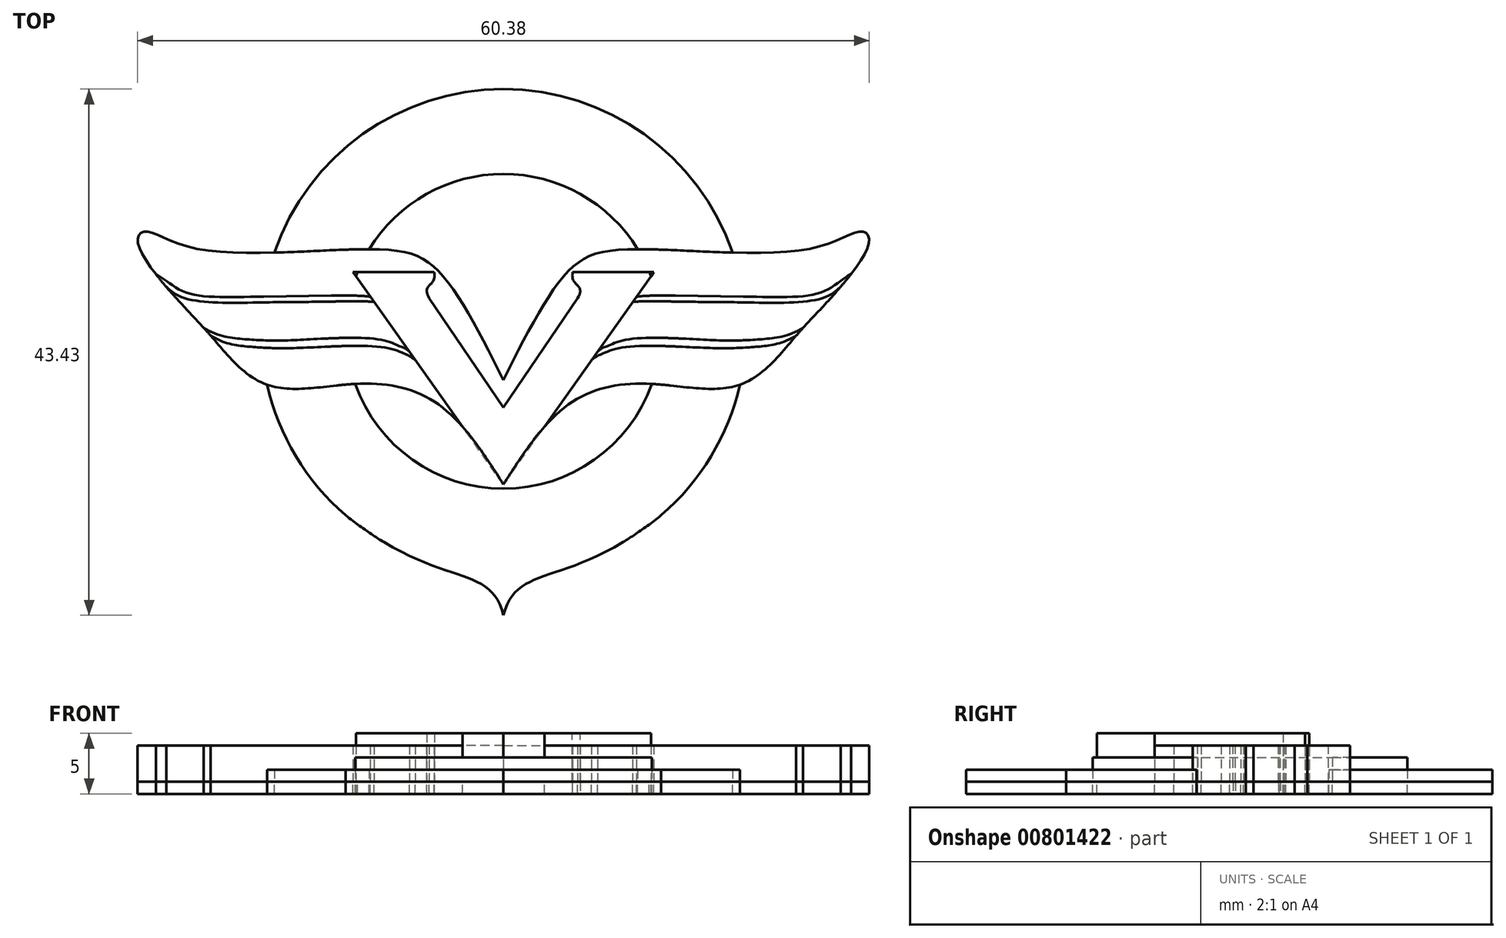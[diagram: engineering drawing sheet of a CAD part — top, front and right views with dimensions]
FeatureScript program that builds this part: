
annotation { "Feature Type Name" : "Feature", "Feature Type Description" : "" }
export const myFeature = defineFeature(function(context is Context, id is Id, definition is map)
    precondition{}
    {
        {
            var Q0;
            Q0=qCreatedBy(makeId("Top.planeOp"),FACE);
            var sketch = newSketch(context, id + "F0", { "sketchPlane" : qUnion([Q0])});
            skCircle(sketch, "E0", {"center": v(31.17, -29.1) * mm, "radius": 20 * mm});
            skFitSpline(sketch, "E1", {"points": [v(31.17, -52.52) * mm, v(44.19, -44.27) * mm], "startDerivative": vector(3.45, 13.39) * mm, "endDerivative": vector(23.34, 18.74) * mm});
            skLineSegment(sketch, "E2", {"start": v(31.17, -52.52) * mm, "end": v(31.17, -29.1) * mm, "construction": true});
            skFitSpline(sketch, "E3.MirrorCS", {"points": [v(31.17, -52.52) * mm, v(18.15, -44.27) * mm], "startDerivative": vector(-3.45, 13.39) * mm, "endDerivative": vector(-23.34, 18.74) * mm});
            skFitSpline(sketch, "E4", {"points": [v(31.17, -33.12) * mm, v(36.42, -24.23) * mm, v(41.17, -22.33) * mm, v(56.67, -22.23) * mm, v(60.84, -20.86) * mm, v(61.35, -21.69) * mm, v(58.45, -26.04) * mm, v(55.24, -29.56) * mm, v(50.68, -33.5) * mm, v(43.26, -33.42) * mm, v(36.77, -34.96) * mm, v(31.17, -41.74) * mm], "startDerivative": vector(45.4, 90.85) * mm, "endDerivative": vector(-47.74, -76.75) * mm});
            skFitSpline(sketch, "E5", {"points": [v(42.15, -26.23) * mm, v(45.57, -26.14) * mm, v(52.5, -26.25) * mm, v(57.51, -25.84) * mm, v(59.86, -24.36) * mm], "startDerivative": vector(15.57, 1.58) * mm, "endDerivative": vector(13.88, 7.6) * mm});
            skFitSpline(sketch, "E6", {"points": [v(38.94, -30.77) * mm, v(39.65, -30.35) * mm, v(41.5, -29.75) * mm, v(48.88, -29.83) * mm, v(52.47, -29.74) * mm, v(55.9, -28.8) * mm], "startDerivative": vector(9.68, 8.92) * mm, "endDerivative": vector(17.36, 10.5) * mm});
            skFitSpline(sketch, "E7.MirrorCS", {"points": [v(31.17, -33.12) * mm, v(25.92, -24.23) * mm, v(21.17, -22.33) * mm, v(5.67, -22.23) * mm, v(1.5, -20.86) * mm, v(0.99, -21.69) * mm, v(3.9, -26.04) * mm, v(7.1, -29.56) * mm, v(11.66, -33.5) * mm, v(19.08, -33.42) * mm, v(25.57, -34.96) * mm, v(31.17, -41.74) * mm], "startDerivative": vector(-45.4, 90.85) * mm, "endDerivative": vector(47.74, -76.75) * mm});
            skFitSpline(sketch, "E8.MirrorCS", {"points": [v(23.4, -30.77) * mm, v(22.69, -30.35) * mm, v(20.85, -29.75) * mm, v(13.46, -29.83) * mm, v(9.87, -29.74) * mm, v(6.43, -28.8) * mm], "startDerivative": vector(-9.68, 8.92) * mm, "endDerivative": vector(-17.36, 10.5) * mm});
            skFitSpline(sketch, "E9.MirrorCS", {"points": [v(20.19, -26.23) * mm, v(16.77, -26.14) * mm, v(9.84, -26.25) * mm, v(4.83, -25.84) * mm, v(2.48, -24.36) * mm], "startDerivative": vector(-15.57, 1.58) * mm, "endDerivative": vector(-13.88, 7.6) * mm});
            skCircle(sketch, "E10", {"center": v(31.17, -29.1) * mm, "radius": 13 * mm});
            skLineSegment(sketch, "E11", {"start": v(31.17, -41.74) * mm, "end": v(18.76, -24.2) * mm});
            skLineSegment(sketch, "E12", {"start": v(18.76, -24.2) * mm, "end": v(25.46, -24.2) * mm});
            skLineSegment(sketch, "E13", {"start": v(31.17, -35.37) * mm, "end": v(25.04, -26.35) * mm});
            skFitSpline(sketch, "E14", {"points": [v(25.04, -26.35) * mm, v(25.46, -24.2) * mm], "startDerivative": vector(-2.08, 3.7) * mm, "endDerivative": vector(-0.66, 3.78) * mm});
            skLineSegment(sketch, "E15.MirrorCS", {"start": v(31.17, -35.37) * mm, "end": v(37.3, -26.35) * mm});
            skFitSpline(sketch, "E16.MirrorCS", {"points": [v(37.3, -26.35) * mm, v(36.88, -24.2) * mm], "startDerivative": vector(2.08, 3.7) * mm, "endDerivative": vector(0.66, 3.78) * mm});
            skLineSegment(sketch, "E17.MirrorCS", {"start": v(43.58, -24.2) * mm, "end": v(36.88, -24.2) * mm});
            skLineSegment(sketch, "E18.MirrorCS", {"start": v(31.17, -41.74) * mm, "end": v(43.58, -24.2) * mm});
            skCircle(sketch, "E19", {"center": v(31.17, -29.1) * mm, "radius": 14.5 * mm});
            skLineSegment(sketch, "E20", {"start": v(31.17, -29.1) * mm, "end": v(31.17, -14.6) * mm, "construction": true});
            skFitSpline(sketch, "E21", {"points": [v(41.84, -26.66) * mm, v(45.46, -26.64) * mm, v(50.26, -26.69) * mm, v(56.4, -26.59) * mm, v(59.57, -24.74) * mm], "startDerivative": vector(15.57, 1.58) * mm, "endDerivative": vector(12.34, 17.15) * mm});
            skFitSpline(sketch, "E22", {"points": [v(38.44, -31.47) * mm, v(39.16, -31.02) * mm, v(41, -30.42) * mm, v(48.39, -30.47) * mm, v(51.98, -30.37) * mm, v(55.33, -29.45) * mm], "startDerivative": vector(9.65, 8.96) * mm, "endDerivative": vector(17.32, 10.56) * mm});
            skFitSpline(sketch, "E23.MirrorCS", {"points": [v(20.5, -26.66) * mm, v(16.88, -26.64) * mm, v(12.08, -26.69) * mm, v(5.95, -26.59) * mm, v(2.77, -24.74) * mm], "startDerivative": vector(-15.57, 1.58) * mm, "endDerivative": vector(-12.34, 17.15) * mm});
            skFitSpline(sketch, "E24.MirrorCS", {"points": [v(23.9, -31.47) * mm, v(23.18, -31.02) * mm, v(21.34, -30.42) * mm, v(13.95, -30.47) * mm, v(10.36, -30.37) * mm, v(7, -29.45) * mm], "startDerivative": vector(-9.65, 8.96) * mm, "endDerivative": vector(-17.32, 10.56) * mm});
            skSolve(sketch);
        }
        {
            var Q0;
            {var subQ0=sQuery(id+"F0.wireOp",EDGE,"E4");var subQ1=sQuery(id+"F0.wireOp",EDGE,"E0");var subQ2=makeQuery(id+"F0.imprint","INTERSECT",VERTEX,{"disambiguationData":[OD(0.0)],"derivedFrom":[subQ1,subQ0]});Q0=makeQuery(id+"F0.imprint","IMPRINT",FACE,{"disambiguationData":[TD([[makeQuery(id+"F0.imprint","IMPRINT",EDGE,{"disambiguationData":[TD([[subQ2,-1.0]])],"derivedFrom":subQ1}),1.0]])]});}
            var Q1;
            {var subQ1=sQuery(id+"F0.wireOp",EDGE,"E0");var subQ6=sQuery(id+"F0.wireOp",EDGE,"E3.MirrorCS");var subQ12=makeQuery(id+"F0.imprint","INTERSECT",VERTEX,{"disambiguationData":[OD(0.0)],"derivedFrom":[subQ1,subQ6]});Q1=makeQuery(id+"F0.imprint","IMPRINT",FACE,{"disambiguationData":[TD([[makeQuery(id+"F0.imprint","IMPRINT",EDGE,{"disambiguationData":[TD([[subQ12,1.0]])],"derivedFrom":subQ1}),1.0]])]});}
            var Q2;
            {var subQ0=sQuery(id+"F0.wireOp",EDGE,"E19");var subQ1=sQuery(id+"F0.wireOp",EDGE,"E4");var subQ2=makeQuery(id+"F0.imprint","INTERSECT",VERTEX,{"disambiguationData":[OD(1.0)],"derivedFrom":[subQ1,subQ0]});Q2=makeQuery(id+"F0.imprint","IMPRINT",FACE,{"disambiguationData":[TD([[makeQuery(id+"F0.imprint","IMPRINT",EDGE,{"disambiguationData":[TD([[subQ2,-1.0]])],"derivedFrom":subQ1}),1.0]])]});}
            var Q3;
            {var subQ0=sQuery(id+"F0.wireOp",EDGE,"E10");var subQ1=sQuery(id+"F0.wireOp",EDGE,"E4");var subQ2=makeQuery(id+"F0.imprint","INTERSECT",VERTEX,{"disambiguationData":[OD(0.0)],"derivedFrom":[subQ1,subQ0]});Q3=makeQuery(id+"F0.imprint","IMPRINT",FACE,{"disambiguationData":[TD([[makeQuery(id+"F0.imprint","IMPRINT",EDGE,{"disambiguationData":[TD([[subQ2,-1.0]])],"derivedFrom":subQ1}),1.0]])]});}
            var Q4;
            {var subQ0=sQuery(id+"F0.wireOp",EDGE,"E3.MirrorCS");var subQ1=sQuery(id+"F0.wireOp",EDGE,"E0");var subQ2=makeQuery(id+"F0.imprint","INTERSECT",VERTEX,{"disambiguationData":[OD(1.0)],"derivedFrom":[subQ1,subQ0]});Q4=makeQuery(id+"F0.imprint","IMPRINT",FACE,{"disambiguationData":[TD([[makeQuery(id+"F0.imprint","IMPRINT",EDGE,{"disambiguationData":[TD([[subQ2,-1.0]])],"derivedFrom":subQ1}),-1.0]])]});}
            extrude(context, id + "F1", {"entities" : qUnion([Q0, Q1, Q2, Q3, Q4]), "depth" : 1 * mm, "offsetDistance" : 25 * mm});
        }
        {
            var Q0;
            {var subQ0=sQuery(id+"F0.wireOp",EDGE,"E7.MirrorCS");var subQ1=sQuery(id+"F0.wireOp",EDGE,"E4");var subQ2=makeQuery(id+"F0.imprint","INTERSECT",VERTEX,{"derivedFrom":[subQ1,subQ0]});Q0=makeQuery(id+"F0.imprint","IMPRINT",FACE,{"disambiguationData":[TD([[makeQuery(id+"F0.imprint","IMPRINT",EDGE,{"disambiguationData":[TD([[subQ2,-1.0]])],"derivedFrom":subQ1}),1.0]])]});}
            var Q1;
            {var subQ0=sQuery(id+"F0.wireOp",EDGE,"E10");var subQ1=sQuery(id+"F0.wireOp",EDGE,"E4");var subQ2=makeQuery(id+"F0.imprint","INTERSECT",VERTEX,{"disambiguationData":[OD(1.0)],"derivedFrom":[subQ1,subQ0]});Q1=makeQuery(id+"F0.imprint","IMPRINT",FACE,{"disambiguationData":[TD([[makeQuery(id+"F0.imprint","IMPRINT",EDGE,{"disambiguationData":[TD([[subQ2,-1.0]])],"derivedFrom":subQ1}),1.0]])]});}
            var Q2;
            {var subQ0=sQuery(id+"F0.wireOp",EDGE,"E18.MirrorCS");var subQ1=sQuery(id+"F0.wireOp",EDGE,"E4");var subQ3=makeQuery(id+"F0.imprint","INTERSECT",VERTEX,{"derivedFrom":[subQ1,subQ0]});Q2=makeQuery(id+"F0.imprint","IMPRINT",FACE,{"disambiguationData":[TD([[makeQuery(id+"F0.imprint","IMPRINT",EDGE,{"disambiguationData":[TD([[subQ3,-1.0]])],"derivedFrom":subQ1}),1.0]])]});}
            var Q3;
            {var subQ0=sQuery(id+"F0.wireOp",EDGE,"E11");var subQ1=sQuery(id+"F0.wireOp",EDGE,"E7.MirrorCS");var subQ3=makeQuery(id+"F0.imprint","INTERSECT",VERTEX,{"derivedFrom":[subQ1,subQ0]});Q3=makeQuery(id+"F0.imprint","IMPRINT",FACE,{"disambiguationData":[TD([[makeQuery(id+"F0.imprint","IMPRINT",EDGE,{"disambiguationData":[TD([[subQ3,-1.0]])],"derivedFrom":subQ1}),-1.0]])]});}
            extrude(context, id + "F2", {"entities" : qUnion([Q0, Q1, Q2, Q3]), "depth" : 2 * mm, "offsetDistance" : 25 * mm});
        }
        {
            var Q0;
            Q0=makeQuery(id+"F0.imprint","IMPRINT",FACE,{"disambiguationData":[TD([[makeQuery(id+"F0.imprint","IMPRINT",EDGE,{"derivedFrom":sQuery(id+"F0.wireOp",EDGE,"E13")}),1.0]])]});
            extrude(context, id + "F3", {"entities" : qUnion([Q0]), "depth" : 4 * mm, "offsetDistance" : 25 * mm});
        }
        {
            var Q0;
            {var subQ0=sQuery(id+"F0.wireOp",EDGE,"E7.MirrorCS");var subQ1=sQuery(id+"F0.wireOp",EDGE,"E0");var subQ2=makeQuery(id+"F0.imprint","INTERSECT",VERTEX,{"disambiguationData":[OD(0.0)],"derivedFrom":[subQ1,subQ0]});Q0=makeQuery(id+"F0.imprint","IMPRINT",FACE,{"disambiguationData":[TD([[makeQuery(id+"F0.imprint","IMPRINT",EDGE,{"disambiguationData":[TD([[subQ2,-1.0]])],"derivedFrom":subQ1}),-1.0]])]});}
            var Q1;
            {var subQ0=sQuery(id+"F0.wireOp",EDGE,"E7.MirrorCS");var subQ1=sQuery(id+"F0.wireOp",EDGE,"E0");var subQ2=makeQuery(id+"F0.imprint","INTERSECT",VERTEX,{"disambiguationData":[OD(0.0)],"derivedFrom":[subQ1,subQ0]});Q1=makeQuery(id+"F0.imprint","IMPRINT",FACE,{"disambiguationData":[TD([[makeQuery(id+"F0.imprint","IMPRINT",EDGE,{"disambiguationData":[TD([[subQ2,-1.0]])],"derivedFrom":subQ1}),1.0]])]});}
            var Q2;
            {var subQ0=sQuery(id+"F0.wireOp",EDGE,"E10");var subQ1=sQuery(id+"F0.wireOp",EDGE,"E7.MirrorCS");var subQ2=makeQuery(id+"F0.imprint","INTERSECT",VERTEX,{"disambiguationData":[OD(0.0)],"derivedFrom":[subQ1,subQ0]});Q2=makeQuery(id+"F0.imprint","IMPRINT",FACE,{"disambiguationData":[TD([[makeQuery(id+"F0.imprint","IMPRINT",EDGE,{"disambiguationData":[TD([[subQ2,-1.0]])],"derivedFrom":subQ1}),1.0]])]});}
            var Q3;
            Q3=makeQuery(id+"F0.imprint","IMPRINT",FACE,{"disambiguationData":[TD([[makeQuery(id+"F0.imprint","IMPRINT",EDGE,{"derivedFrom":sQuery(id+"F0.wireOp",EDGE,"E13")}),-1.0]])]});
            var Q4;
            {var subQ0=sQuery(id+"F0.wireOp",EDGE,"E11");var subQ1=sQuery(id+"F0.wireOp",EDGE,"E9.MirrorCS");var subQ2=makeQuery(id+"F0.imprint","INTERSECT",VERTEX,{"derivedFrom":[subQ1,subQ0]});Q4=makeQuery(id+"F0.imprint","IMPRINT",FACE,{"disambiguationData":[TD([[makeQuery(id+"F0.imprint","IMPRINT",EDGE,{"disambiguationData":[TD([[subQ2,-1.0]])],"derivedFrom":subQ1}),-1.0]])]});}
            var Q5;
            {var subQ0=sQuery(id+"F0.wireOp",EDGE,"E23.MirrorCS");var subQ1=sQuery(id+"F0.wireOp",EDGE,"E0");var subQ2=makeQuery(id+"F0.imprint","INTERSECT",VERTEX,{"derivedFrom":[subQ1,subQ0]});Q5=makeQuery(id+"F0.imprint","IMPRINT",FACE,{"disambiguationData":[TD([[makeQuery(id+"F0.imprint","IMPRINT",EDGE,{"disambiguationData":[TD([[subQ2,-1.0]])],"derivedFrom":subQ1}),1.0]])]});}
            var Q6;
            {var subQ0=sQuery(id+"F0.wireOp",EDGE,"E10");var subQ1=sQuery(id+"F0.wireOp",EDGE,"E8.MirrorCS");var subQ2=makeQuery(id+"F0.imprint","INTERSECT",VERTEX,{"derivedFrom":[subQ1,subQ0]});Q6=makeQuery(id+"F0.imprint","IMPRINT",FACE,{"disambiguationData":[TD([[makeQuery(id+"F0.imprint","IMPRINT",EDGE,{"disambiguationData":[TD([[subQ2,-1.0]])],"derivedFrom":subQ1}),-1.0]])]});}
            var Q7;
            {var subQ0=sQuery(id+"F0.wireOp",EDGE,"E11");var subQ1=sQuery(id+"F0.wireOp",EDGE,"E8.MirrorCS");var subQ2=makeQuery(id+"F0.imprint","INTERSECT",VERTEX,{"derivedFrom":[subQ1,subQ0]});Q7=makeQuery(id+"F0.imprint","IMPRINT",FACE,{"disambiguationData":[TD([[makeQuery(id+"F0.imprint","IMPRINT",EDGE,{"disambiguationData":[TD([[subQ2,-1.0]])],"derivedFrom":subQ1}),-1.0]])]});}
            var Q8;
            {var subQ0=sQuery(id+"F0.wireOp",EDGE,"E10");var subQ1=sQuery(id+"F0.wireOp",EDGE,"E7.MirrorCS");var subQ2=makeQuery(id+"F0.imprint","INTERSECT",VERTEX,{"disambiguationData":[OD(1.0)],"derivedFrom":[subQ1,subQ0]});Q8=makeQuery(id+"F0.imprint","IMPRINT",FACE,{"disambiguationData":[TD([[makeQuery(id+"F0.imprint","IMPRINT",EDGE,{"disambiguationData":[TD([[subQ2,-1.0]])],"derivedFrom":subQ1}),1.0]])]});}
            var Q9;
            {var subQ0=sQuery(id+"F0.wireOp",EDGE,"E19");var subQ1=sQuery(id+"F0.wireOp",EDGE,"E7.MirrorCS");var subQ2=makeQuery(id+"F0.imprint","INTERSECT",VERTEX,{"disambiguationData":[OD(1.0)],"derivedFrom":[subQ1,subQ0]});Q9=makeQuery(id+"F0.imprint","IMPRINT",FACE,{"disambiguationData":[TD([[makeQuery(id+"F0.imprint","IMPRINT",EDGE,{"disambiguationData":[TD([[subQ2,-1.0]])],"derivedFrom":subQ1}),1.0]])]});}
            var Q10;
            {var subQ0=sQuery(id+"F0.wireOp",EDGE,"E24.MirrorCS");var subQ1=sQuery(id+"F0.wireOp",EDGE,"E0");var subQ2=makeQuery(id+"F0.imprint","INTERSECT",VERTEX,{"derivedFrom":[subQ1,subQ0]});Q10=makeQuery(id+"F0.imprint","IMPRINT",FACE,{"disambiguationData":[TD([[makeQuery(id+"F0.imprint","IMPRINT",EDGE,{"disambiguationData":[TD([[subQ2,-1.0]])],"derivedFrom":subQ1}),1.0]])]});}
            var Q11;
            {var subQ0=sQuery(id+"F0.wireOp",EDGE,"E10");var subQ1=sQuery(id+"F0.wireOp",EDGE,"E4");var subQ2=makeQuery(id+"F0.imprint","INTERSECT",VERTEX,{"disambiguationData":[OD(1.0)],"derivedFrom":[subQ1,subQ0]});Q11=makeQuery(id+"F0.imprint","IMPRINT",FACE,{"disambiguationData":[TD([[makeQuery(id+"F0.imprint","IMPRINT",EDGE,{"disambiguationData":[TD([[subQ2,-1.0]])],"derivedFrom":subQ1}),-1.0]])]});}
            var Q12;
            {var subQ0=sQuery(id+"F0.wireOp",EDGE,"E18.MirrorCS");var subQ1=sQuery(id+"F0.wireOp",EDGE,"E6");var subQ2=makeQuery(id+"F0.imprint","INTERSECT",VERTEX,{"derivedFrom":[subQ1,subQ0]});Q12=makeQuery(id+"F0.imprint","IMPRINT",FACE,{"disambiguationData":[TD([[makeQuery(id+"F0.imprint","IMPRINT",EDGE,{"disambiguationData":[TD([[subQ2,-1.0]])],"derivedFrom":subQ1}),1.0]])]});}
            var Q13;
            {var subQ0=sQuery(id+"F0.wireOp",EDGE,"E18.MirrorCS");var subQ1=sQuery(id+"F0.wireOp",EDGE,"E5");var subQ2=makeQuery(id+"F0.imprint","INTERSECT",VERTEX,{"derivedFrom":[subQ1,subQ0]});Q13=makeQuery(id+"F0.imprint","IMPRINT",FACE,{"disambiguationData":[TD([[makeQuery(id+"F0.imprint","IMPRINT",EDGE,{"disambiguationData":[TD([[subQ2,-1.0]])],"derivedFrom":subQ1}),1.0]])]});}
            var Q14;
            {var subQ0=sQuery(id+"F0.wireOp",EDGE,"E10");var subQ1=sQuery(id+"F0.wireOp",EDGE,"E4");var subQ2=makeQuery(id+"F0.imprint","INTERSECT",VERTEX,{"disambiguationData":[OD(0.0)],"derivedFrom":[subQ1,subQ0]});Q14=makeQuery(id+"F0.imprint","IMPRINT",FACE,{"disambiguationData":[TD([[makeQuery(id+"F0.imprint","IMPRINT",EDGE,{"disambiguationData":[TD([[subQ2,-1.0]])],"derivedFrom":subQ1}),-1.0]])]});}
            var Q15;
            {var subQ0=sQuery(id+"F0.wireOp",EDGE,"E4");var subQ1=sQuery(id+"F0.wireOp",EDGE,"E0");var subQ2=makeQuery(id+"F0.imprint","INTERSECT",VERTEX,{"disambiguationData":[OD(0.0)],"derivedFrom":[subQ1,subQ0]});Q15=makeQuery(id+"F0.imprint","IMPRINT",FACE,{"disambiguationData":[TD([[makeQuery(id+"F0.imprint","IMPRINT",EDGE,{"disambiguationData":[TD([[subQ2,1.0]])],"derivedFrom":subQ1}),1.0]])]});}
            var Q16;
            {var subQ0=sQuery(id+"F0.wireOp",EDGE,"E10");var subQ1=sQuery(id+"F0.wireOp",EDGE,"E6");var subQ2=makeQuery(id+"F0.imprint","INTERSECT",VERTEX,{"derivedFrom":[subQ1,subQ0]});Q16=makeQuery(id+"F0.imprint","IMPRINT",FACE,{"disambiguationData":[TD([[makeQuery(id+"F0.imprint","IMPRINT",EDGE,{"disambiguationData":[TD([[subQ2,-1.0]])],"derivedFrom":subQ1}),1.0]])]});}
            var Q17;
            {var subQ0=sQuery(id+"F0.wireOp",EDGE,"E21");var subQ1=sQuery(id+"F0.wireOp",EDGE,"E0");var subQ2=makeQuery(id+"F0.imprint","INTERSECT",VERTEX,{"derivedFrom":[subQ1,subQ0]});Q17=makeQuery(id+"F0.imprint","IMPRINT",FACE,{"disambiguationData":[TD([[makeQuery(id+"F0.imprint","IMPRINT",EDGE,{"disambiguationData":[TD([[subQ2,1.0]])],"derivedFrom":subQ1}),1.0]])]});}
            var Q18;
            {var subQ0=sQuery(id+"F0.wireOp",EDGE,"E19");var subQ1=sQuery(id+"F0.wireOp",EDGE,"E4");var subQ2=makeQuery(id+"F0.imprint","INTERSECT",VERTEX,{"disambiguationData":[OD(1.0)],"derivedFrom":[subQ1,subQ0]});Q18=makeQuery(id+"F0.imprint","IMPRINT",FACE,{"disambiguationData":[TD([[makeQuery(id+"F0.imprint","IMPRINT",EDGE,{"disambiguationData":[TD([[subQ2,-1.0]])],"derivedFrom":subQ1}),-1.0]])]});}
            var Q19;
            {var subQ0=sQuery(id+"F0.wireOp",EDGE,"E4");var subQ1=sQuery(id+"F0.wireOp",EDGE,"E0");var subQ2=makeQuery(id+"F0.imprint","INTERSECT",VERTEX,{"disambiguationData":[OD(1.0)],"derivedFrom":[subQ1,subQ0]});Q19=makeQuery(id+"F0.imprint","IMPRINT",FACE,{"disambiguationData":[TD([[makeQuery(id+"F0.imprint","IMPRINT",EDGE,{"disambiguationData":[TD([[subQ2,-1.0]])],"derivedFrom":subQ1}),1.0]])]});}
            var Q20;
            {var subQ0=sQuery(id+"F0.wireOp",EDGE,"E4");var subQ1=sQuery(id+"F0.wireOp",EDGE,"E0");var subQ2=makeQuery(id+"F0.imprint","INTERSECT",VERTEX,{"disambiguationData":[OD(0.0)],"derivedFrom":[subQ1,subQ0]});Q20=makeQuery(id+"F0.imprint","IMPRINT",FACE,{"disambiguationData":[TD([[makeQuery(id+"F0.imprint","IMPRINT",EDGE,{"disambiguationData":[TD([[subQ2,1.0]])],"derivedFrom":subQ1}),-1.0]])]});}
            var Q21;
            {var subQ0=sQuery(id+"F0.wireOp",EDGE,"E21");var subQ1=sQuery(id+"F0.wireOp",EDGE,"E0");var subQ2=makeQuery(id+"F0.imprint","INTERSECT",VERTEX,{"derivedFrom":[subQ1,subQ0]});Q21=makeQuery(id+"F0.imprint","IMPRINT",FACE,{"disambiguationData":[TD([[makeQuery(id+"F0.imprint","IMPRINT",EDGE,{"disambiguationData":[TD([[subQ2,1.0]])],"derivedFrom":subQ1}),-1.0]])]});}
            var Q22;
            {var subQ0=sQuery(id+"F0.wireOp",EDGE,"E4");var subQ1=sQuery(id+"F0.wireOp",EDGE,"E0");var subQ2=makeQuery(id+"F0.imprint","INTERSECT",VERTEX,{"disambiguationData":[OD(1.0)],"derivedFrom":[subQ1,subQ0]});Q22=makeQuery(id+"F0.imprint","IMPRINT",FACE,{"disambiguationData":[TD([[makeQuery(id+"F0.imprint","IMPRINT",EDGE,{"disambiguationData":[TD([[subQ2,-1.0]])],"derivedFrom":subQ1}),-1.0]])]});}
            var Q23;
            {var subQ0=sQuery(id+"F0.wireOp",EDGE,"E23.MirrorCS");var subQ1=sQuery(id+"F0.wireOp",EDGE,"E0");var subQ2=makeQuery(id+"F0.imprint","INTERSECT",VERTEX,{"derivedFrom":[subQ1,subQ0]});Q23=makeQuery(id+"F0.imprint","IMPRINT",FACE,{"disambiguationData":[TD([[makeQuery(id+"F0.imprint","IMPRINT",EDGE,{"disambiguationData":[TD([[subQ2,-1.0]])],"derivedFrom":subQ1}),-1.0]])]});}
            var Q24;
            {var subQ0=sQuery(id+"F0.wireOp",EDGE,"E7.MirrorCS");var subQ1=sQuery(id+"F0.wireOp",EDGE,"E0");var subQ2=makeQuery(id+"F0.imprint","INTERSECT",VERTEX,{"disambiguationData":[OD(1.0)],"derivedFrom":[subQ1,subQ0]});Q24=makeQuery(id+"F0.imprint","IMPRINT",FACE,{"disambiguationData":[TD([[makeQuery(id+"F0.imprint","IMPRINT",EDGE,{"disambiguationData":[TD([[subQ2,1.0]])],"derivedFrom":subQ1}),-1.0]])]});}
            extrude(context, id + "F4", {"entities" : qUnion([Q0, Q1, Q2, Q3, Q4, Q5, Q6, Q7, Q8, Q9, Q10, Q11, Q12, Q13, Q14, Q15, Q16, Q17, Q18, Q19, Q20, Q21, Q22, Q23, Q24]), "depth" : 3 * mm, "offsetDistance" : 25 * mm});
        }
        {
            var Q0;
            Q0=makeQuery(id+"F1.opExtrude","CAP_FACE",FACE,{"disambiguationData":[OSD([sQuery(id+"F0.wireOp",EDGE,"E0"),sQuery(id+"F0.wireOp",EDGE,"E1"),sQuery(id+"F0.wireOp",EDGE,"E3.MirrorCS"),sQuery(id+"F0.wireOp",EDGE,"E4"),sQuery(id+"F0.wireOp",EDGE,"E7.MirrorCS"),sQuery(id+"F0.wireOp",EDGE,"E10")])],"isStart":true});
            var Q1;
            Q1=makeQuery(id+"F2.opExtrude","CAP_FACE",FACE,{"disambiguationData":[OSD([sQuery(id+"F0.wireOp",EDGE,"E4"),sQuery(id+"F0.wireOp",EDGE,"E7.MirrorCS"),sQuery(id+"F0.wireOp",EDGE,"E10"),sQuery(id+"F0.wireOp",EDGE,"E11"),sQuery(id+"F0.wireOp",EDGE,"E18.MirrorCS")])],"isStart":true});
            var Q2;
            Q2=makeQuery(id+"F3.opExtrude","CAP_FACE",FACE,{"disambiguationData":[OSD([sQuery(id+"F0.wireOp",EDGE,"E4"),sQuery(id+"F0.wireOp",EDGE,"E7.MirrorCS"),sQuery(id+"F0.wireOp",EDGE,"E10"),sQuery(id+"F0.wireOp",EDGE,"E11"),sQuery(id+"F0.wireOp",EDGE,"E12"),sQuery(id+"F0.wireOp",EDGE,"E13"),sQuery(id+"F0.wireOp",EDGE,"E14"),sQuery(id+"F0.wireOp",EDGE,"E15.MirrorCS"),sQuery(id+"F0.wireOp",EDGE,"E16.MirrorCS"),sQuery(id+"F0.wireOp",EDGE,"E17.MirrorCS"),sQuery(id+"F0.wireOp",EDGE,"E18.MirrorCS")])],"isStart":true});
            var Q3;
            Q3=makeQuery(id+"F4.opExtrude","CAP_FACE",FACE,{"disambiguationData":[OSD([sQuery(id+"F0.wireOp",EDGE,"E7.MirrorCS"),sQuery(id+"F0.wireOp",EDGE,"E11"),sQuery(id+"F0.wireOp",EDGE,"E24.MirrorCS")])],"isStart":true});
            var Q4;
            Q4=makeQuery(id+"F4.opExtrude","CAP_FACE",FACE,{"disambiguationData":[OSD([sQuery(id+"F0.wireOp",EDGE,"E7.MirrorCS"),sQuery(id+"F0.wireOp",EDGE,"E8.MirrorCS"),sQuery(id+"F0.wireOp",EDGE,"E11"),sQuery(id+"F0.wireOp",EDGE,"E23.MirrorCS")])],"isStart":true});
            var Q5;
            Q5=makeQuery(id+"F4.opExtrude","CAP_FACE",FACE,{"disambiguationData":[OSD([sQuery(id+"F0.wireOp",EDGE,"E4"),sQuery(id+"F0.wireOp",EDGE,"E5"),sQuery(id+"F0.wireOp",EDGE,"E7.MirrorCS"),sQuery(id+"F0.wireOp",EDGE,"E9.MirrorCS"),sQuery(id+"F0.wireOp",EDGE,"E11"),sQuery(id+"F0.wireOp",EDGE,"E12"),sQuery(id+"F0.wireOp",EDGE,"E13"),sQuery(id+"F0.wireOp",EDGE,"E14"),sQuery(id+"F0.wireOp",EDGE,"E15.MirrorCS"),sQuery(id+"F0.wireOp",EDGE,"E16.MirrorCS"),sQuery(id+"F0.wireOp",EDGE,"E17.MirrorCS"),sQuery(id+"F0.wireOp",EDGE,"E18.MirrorCS")])],"isStart":true});
            var Q6;
            Q6=makeQuery(id+"F4.opExtrude","CAP_FACE",FACE,{"disambiguationData":[OSD([sQuery(id+"F0.wireOp",EDGE,"E4"),sQuery(id+"F0.wireOp",EDGE,"E6"),sQuery(id+"F0.wireOp",EDGE,"E18.MirrorCS"),sQuery(id+"F0.wireOp",EDGE,"E21")])],"isStart":true});
            var Q7;
            Q7=makeQuery(id+"F2.opExtrude","CAP_FACE",FACE,{"disambiguationData":[OSD([sQuery(id+"F0.wireOp",EDGE,"E4"),sQuery(id+"F0.wireOp",EDGE,"E7.MirrorCS"),sQuery(id+"F0.wireOp",EDGE,"E10")])],"isStart":true});
            var Q8;
            Q8=makeQuery(id+"F1.opExtrude","CAP_FACE",FACE,{"disambiguationData":[OSD([sQuery(id+"F0.wireOp",EDGE,"E0"),sQuery(id+"F0.wireOp",EDGE,"E4"),sQuery(id+"F0.wireOp",EDGE,"E7.MirrorCS"),sQuery(id+"F0.wireOp",EDGE,"E10")])],"isStart":true});
            var Q9;
            Q9=makeQuery(id+"F4.opExtrude","CAP_FACE",FACE,{"disambiguationData":[OSD([sQuery(id+"F0.wireOp",EDGE,"E4"),sQuery(id+"F0.wireOp",EDGE,"E18.MirrorCS"),sQuery(id+"F0.wireOp",EDGE,"E22")])],"isStart":true});
            var Q10;
            {var subQ0=sQuery(id+"F0.wireOp",EDGE,"E22");var subQ1=sQuery(id+"F0.wireOp",EDGE,"E0");var subQ2=makeQuery(id+"F0.imprint","INTERSECT",VERTEX,{"derivedFrom":[subQ1,subQ0]});Q10=makeQuery(id+"F0.imprint","IMPRINT",FACE,{"disambiguationData":[TD([[makeQuery(id+"F0.imprint","IMPRINT",EDGE,{"disambiguationData":[TD([[subQ2,-1.0]])],"derivedFrom":subQ1}),-1.0]])]});}
            var Q11;
            {var subQ0=sQuery(id+"F0.wireOp",EDGE,"E22");var subQ1=sQuery(id+"F0.wireOp",EDGE,"E0");var subQ2=makeQuery(id+"F0.imprint","INTERSECT",VERTEX,{"derivedFrom":[subQ1,subQ0]});Q11=makeQuery(id+"F0.imprint","IMPRINT",FACE,{"disambiguationData":[TD([[makeQuery(id+"F0.imprint","IMPRINT",EDGE,{"disambiguationData":[TD([[subQ2,-1.0]])],"derivedFrom":subQ1}),1.0]])]});}
            var Q12;
            {var subQ0=sQuery(id+"F0.wireOp",EDGE,"E10");var subQ1=sQuery(id+"F0.wireOp",EDGE,"E6");var subQ2=makeQuery(id+"F0.imprint","INTERSECT",VERTEX,{"derivedFrom":[subQ1,subQ0]});Q12=makeQuery(id+"F0.imprint","IMPRINT",FACE,{"disambiguationData":[TD([[makeQuery(id+"F0.imprint","IMPRINT",EDGE,{"disambiguationData":[TD([[subQ2,-1.0]])],"derivedFrom":subQ1}),-1.0]])]});}
            var Q13;
            {var subQ0=sQuery(id+"F0.wireOp",EDGE,"E18.MirrorCS");var subQ1=sQuery(id+"F0.wireOp",EDGE,"E6");var subQ2=makeQuery(id+"F0.imprint","INTERSECT",VERTEX,{"derivedFrom":[subQ1,subQ0]});Q13=makeQuery(id+"F0.imprint","IMPRINT",FACE,{"disambiguationData":[TD([[makeQuery(id+"F0.imprint","IMPRINT",EDGE,{"disambiguationData":[TD([[subQ2,-1.0]])],"derivedFrom":subQ1}),-1.0]])]});}
            var Q14;
            {var subQ0=sQuery(id+"F0.wireOp",EDGE,"E11");var subQ1=sQuery(id+"F0.wireOp",EDGE,"E8.MirrorCS");var subQ2=makeQuery(id+"F0.imprint","INTERSECT",VERTEX,{"derivedFrom":[subQ1,subQ0]});Q14=makeQuery(id+"F0.imprint","IMPRINT",FACE,{"disambiguationData":[TD([[makeQuery(id+"F0.imprint","IMPRINT",EDGE,{"disambiguationData":[TD([[subQ2,-1.0]])],"derivedFrom":subQ1}),1.0]])]});}
            var Q15;
            {var subQ0=sQuery(id+"F0.wireOp",EDGE,"E10");var subQ1=sQuery(id+"F0.wireOp",EDGE,"E8.MirrorCS");var subQ2=makeQuery(id+"F0.imprint","INTERSECT",VERTEX,{"derivedFrom":[subQ1,subQ0]});Q15=makeQuery(id+"F0.imprint","IMPRINT",FACE,{"disambiguationData":[TD([[makeQuery(id+"F0.imprint","IMPRINT",EDGE,{"disambiguationData":[TD([[subQ2,-1.0]])],"derivedFrom":subQ1}),1.0]])]});}
            var Q16;
            {var subQ0=sQuery(id+"F0.wireOp",EDGE,"E8.MirrorCS");var subQ1=sQuery(id+"F0.wireOp",EDGE,"E0");var subQ2=makeQuery(id+"F0.imprint","INTERSECT",VERTEX,{"derivedFrom":[subQ1,subQ0]});Q16=makeQuery(id+"F0.imprint","IMPRINT",FACE,{"disambiguationData":[TD([[makeQuery(id+"F0.imprint","IMPRINT",EDGE,{"disambiguationData":[TD([[subQ2,-1.0]])],"derivedFrom":subQ1}),1.0]])]});}
            var Q17;
            {var subQ0=sQuery(id+"F0.wireOp",EDGE,"E8.MirrorCS");var subQ1=sQuery(id+"F0.wireOp",EDGE,"E0");var subQ2=makeQuery(id+"F0.imprint","INTERSECT",VERTEX,{"derivedFrom":[subQ1,subQ0]});Q17=makeQuery(id+"F0.imprint","IMPRINT",FACE,{"disambiguationData":[TD([[makeQuery(id+"F0.imprint","IMPRINT",EDGE,{"disambiguationData":[TD([[subQ2,-1.0]])],"derivedFrom":subQ1}),-1.0]])]});}
            var Q18;
            {var subQ0=sQuery(id+"F0.wireOp",EDGE,"E5");var subQ3=sQuery(id+"F0.wireOp",EDGE,"E0");var subQ4=makeQuery(id+"F0.imprint","INTERSECT",VERTEX,{"derivedFrom":[subQ3,subQ0]});Q18=makeQuery(id+"F0.imprint","IMPRINT",FACE,{"disambiguationData":[TD([[makeQuery(id+"F0.imprint","IMPRINT",EDGE,{"disambiguationData":[TD([[subQ4,1.0]])],"derivedFrom":subQ3}),-1.0]])]});}
            var Q19;
            {var subQ0=sQuery(id+"F0.wireOp",EDGE,"E5");var subQ1=sQuery(id+"F0.wireOp",EDGE,"E0");var subQ2=makeQuery(id+"F0.imprint","INTERSECT",VERTEX,{"derivedFrom":[subQ1,subQ0]});Q19=makeQuery(id+"F0.imprint","IMPRINT",FACE,{"disambiguationData":[TD([[makeQuery(id+"F0.imprint","IMPRINT",EDGE,{"disambiguationData":[TD([[subQ2,1.0]])],"derivedFrom":subQ1}),1.0]])]});}
            var Q20;
            {var subQ0=sQuery(id+"F0.wireOp",EDGE,"E10");var subQ1=sQuery(id+"F0.wireOp",EDGE,"E5");var subQ2=makeQuery(id+"F0.imprint","INTERSECT",VERTEX,{"derivedFrom":[subQ1,subQ0]});Q20=makeQuery(id+"F0.imprint","IMPRINT",FACE,{"disambiguationData":[TD([[makeQuery(id+"F0.imprint","IMPRINT",EDGE,{"disambiguationData":[TD([[subQ2,-1.0]])],"derivedFrom":subQ1}),-1.0]])]});}
            var Q21;
            {var subQ0=sQuery(id+"F0.wireOp",EDGE,"E18.MirrorCS");var subQ1=sQuery(id+"F0.wireOp",EDGE,"E5");var subQ2=makeQuery(id+"F0.imprint","INTERSECT",VERTEX,{"derivedFrom":[subQ1,subQ0]});Q21=makeQuery(id+"F0.imprint","IMPRINT",FACE,{"disambiguationData":[TD([[makeQuery(id+"F0.imprint","IMPRINT",EDGE,{"disambiguationData":[TD([[subQ2,-1.0]])],"derivedFrom":subQ1}),-1.0]])]});}
            var Q22;
            {var subQ0=sQuery(id+"F0.wireOp",EDGE,"E11");var subQ1=sQuery(id+"F0.wireOp",EDGE,"E9.MirrorCS");var subQ2=makeQuery(id+"F0.imprint","INTERSECT",VERTEX,{"derivedFrom":[subQ1,subQ0]});Q22=makeQuery(id+"F0.imprint","IMPRINT",FACE,{"disambiguationData":[TD([[makeQuery(id+"F0.imprint","IMPRINT",EDGE,{"disambiguationData":[TD([[subQ2,-1.0]])],"derivedFrom":subQ1}),1.0]])]});}
            var Q23;
            {var subQ0=sQuery(id+"F0.wireOp",EDGE,"E10");var subQ1=sQuery(id+"F0.wireOp",EDGE,"E9.MirrorCS");var subQ2=makeQuery(id+"F0.imprint","INTERSECT",VERTEX,{"derivedFrom":[subQ1,subQ0]});Q23=makeQuery(id+"F0.imprint","IMPRINT",FACE,{"disambiguationData":[TD([[makeQuery(id+"F0.imprint","IMPRINT",EDGE,{"disambiguationData":[TD([[subQ2,-1.0]])],"derivedFrom":subQ1}),1.0]])]});}
            var Q24;
            {var subQ0=sQuery(id+"F0.wireOp",EDGE,"E9.MirrorCS");var subQ1=sQuery(id+"F0.wireOp",EDGE,"E0");var subQ2=makeQuery(id+"F0.imprint","INTERSECT",VERTEX,{"derivedFrom":[subQ1,subQ0]});Q24=makeQuery(id+"F0.imprint","IMPRINT",FACE,{"disambiguationData":[TD([[makeQuery(id+"F0.imprint","IMPRINT",EDGE,{"disambiguationData":[TD([[subQ2,-1.0]])],"derivedFrom":subQ1}),1.0]])]});}
            var Q25;
            {var subQ0=sQuery(id+"F0.wireOp",EDGE,"E12");var subQ1=sQuery(id+"F0.wireOp",EDGE,"E10");var subQ2=makeQuery(id+"F0.imprint","INTERSECT",VERTEX,{"derivedFrom":[subQ1,subQ0]});Q25=makeQuery(id+"F0.imprint","IMPRINT",FACE,{"disambiguationData":[TD([[makeQuery(id+"F0.imprint","IMPRINT",EDGE,{"disambiguationData":[TD([[subQ2,-1.0]])],"derivedFrom":subQ1}),-1.0]])]});}
            var Q26;
            {var subQ0=sQuery(id+"F0.wireOp",EDGE,"E9.MirrorCS");var subQ3=sQuery(id+"F0.wireOp",EDGE,"E0");var subQ4=makeQuery(id+"F0.imprint","INTERSECT",VERTEX,{"derivedFrom":[subQ3,subQ0]});Q26=makeQuery(id+"F0.imprint","IMPRINT",FACE,{"disambiguationData":[TD([[makeQuery(id+"F0.imprint","IMPRINT",EDGE,{"disambiguationData":[TD([[subQ4,-1.0]])],"derivedFrom":subQ3}),-1.0]])]});}
            var Q27;
            {var subQ0=sQuery(id+"F0.wireOp",EDGE,"E18.MirrorCS");var subQ1=sQuery(id+"F0.wireOp",EDGE,"E10");var subQ2=makeQuery(id+"F0.imprint","INTERSECT",VERTEX,{"derivedFrom":[subQ1,subQ0]});Q27=makeQuery(id+"F0.imprint","IMPRINT",FACE,{"disambiguationData":[TD([[makeQuery(id+"F0.imprint","IMPRINT",EDGE,{"disambiguationData":[TD([[subQ2,-1.0]])],"derivedFrom":subQ1}),-1.0]])]});}
            var Q28;
            {var subQ0=sQuery(id+"F0.wireOp",EDGE,"E11");var subQ1=sQuery(id+"F0.wireOp",EDGE,"E7.MirrorCS");var subQ3=makeQuery(id+"F0.imprint","INTERSECT",VERTEX,{"derivedFrom":[subQ1,subQ0]});Q28=makeQuery(id+"F0.imprint","IMPRINT",FACE,{"disambiguationData":[TD([[makeQuery(id+"F0.imprint","IMPRINT",EDGE,{"disambiguationData":[TD([[subQ3,-1.0]])],"derivedFrom":subQ1}),-1.0]])]});}
            var Q29;
            {var subQ0=sQuery(id+"F0.wireOp",EDGE,"E18.MirrorCS");var subQ1=sQuery(id+"F0.wireOp",EDGE,"E4");var subQ3=makeQuery(id+"F0.imprint","INTERSECT",VERTEX,{"derivedFrom":[subQ1,subQ0]});Q29=makeQuery(id+"F0.imprint","IMPRINT",FACE,{"disambiguationData":[TD([[makeQuery(id+"F0.imprint","IMPRINT",EDGE,{"disambiguationData":[TD([[subQ3,-1.0]])],"derivedFrom":subQ1}),1.0]])]});}
            extrude(context, id + "F5", {"entities" : qUnion([Q0, Q1, Q2, Q3, Q4, Q5, Q6, Q7, Q8, Q9, Q10, Q11, Q12, Q13, Q14, Q15, Q16, Q17, Q18, Q19, Q20, Q21, Q22, Q23, Q24, Q25, Q26, Q27, Q28, Q29]), "depth" : 1 * mm, "offsetDistance" : 25 * mm});
        }
    });
